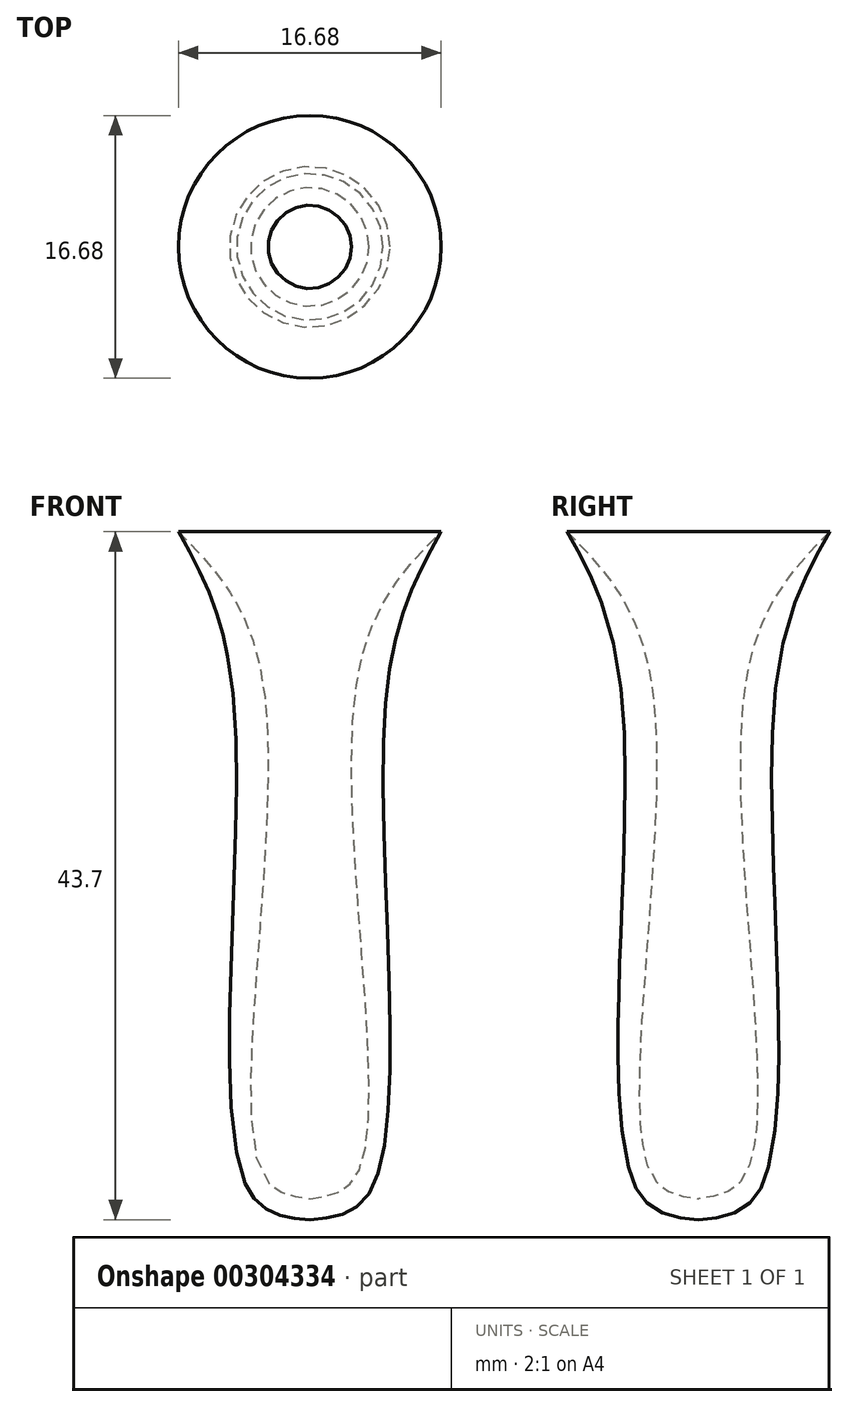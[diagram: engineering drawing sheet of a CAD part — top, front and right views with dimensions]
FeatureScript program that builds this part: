
annotation { "Feature Type Name" : "Feature", "Feature Type Description" : "" }
export const myFeature = defineFeature(function(context is Context, id is Id, definition is map)
    precondition{}
    {
        {
            var Q0;
            Q0=qCreatedBy(makeId("Front.planeOp"),FACE);
            var sketch = newSketch(context, id + "F0", { "sketchPlane" : qUnion([Q0])});
            skFitSpline(sketch, "E0", {"points": [v(0, 0) * mm, v(4.03, 2.15) * mm, v(4.8, 32.55) * mm, v(8.34, 43.7) * mm], "startDerivative": vector(24.42, 2.07) * mm, "endDerivative": vector(15.13, 26.84) * mm});
            skFitSpline(sketch, "E1", {"points": [v(0, 1.33) * mm, v(3.2, 3.3) * mm, v(2.89, 33.46) * mm, v(8.34, 43.7) * mm], "startDerivative": vector(21.41, 2.65) * mm, "endDerivative": vector(22.71, 22.88) * mm});
            skLineSegment(sketch, "E2", {"start": v(0, 0) * mm, "end": v(0, 14.12) * mm, "construction": true});
            skLineSegment(sketch, "E3", {"start": v(0, 0) * mm, "end": v(0, 1.33) * mm});
            skSolve(sketch);
        }
        {
            var Q0;
            Q0=makeQuery(id+"F0.imprint","IMPRINT",FACE,{"disambiguationData":[TD([[makeQuery(id+"F0.imprint","IMPRINT",EDGE,{"derivedFrom":sQuery(id+"F0.wireOp",EDGE,"E0")}),1.0]])]});
            var Q1;
            Q1=sQuery(id+"F0.wireOp",EDGE,"E2");
            revolve(context, id + "F1", {"entities" : qUnion([Q0]), "axis" : qUnion([Q1]), "revolveType" : RevolveType.FULL});
        }
    });
